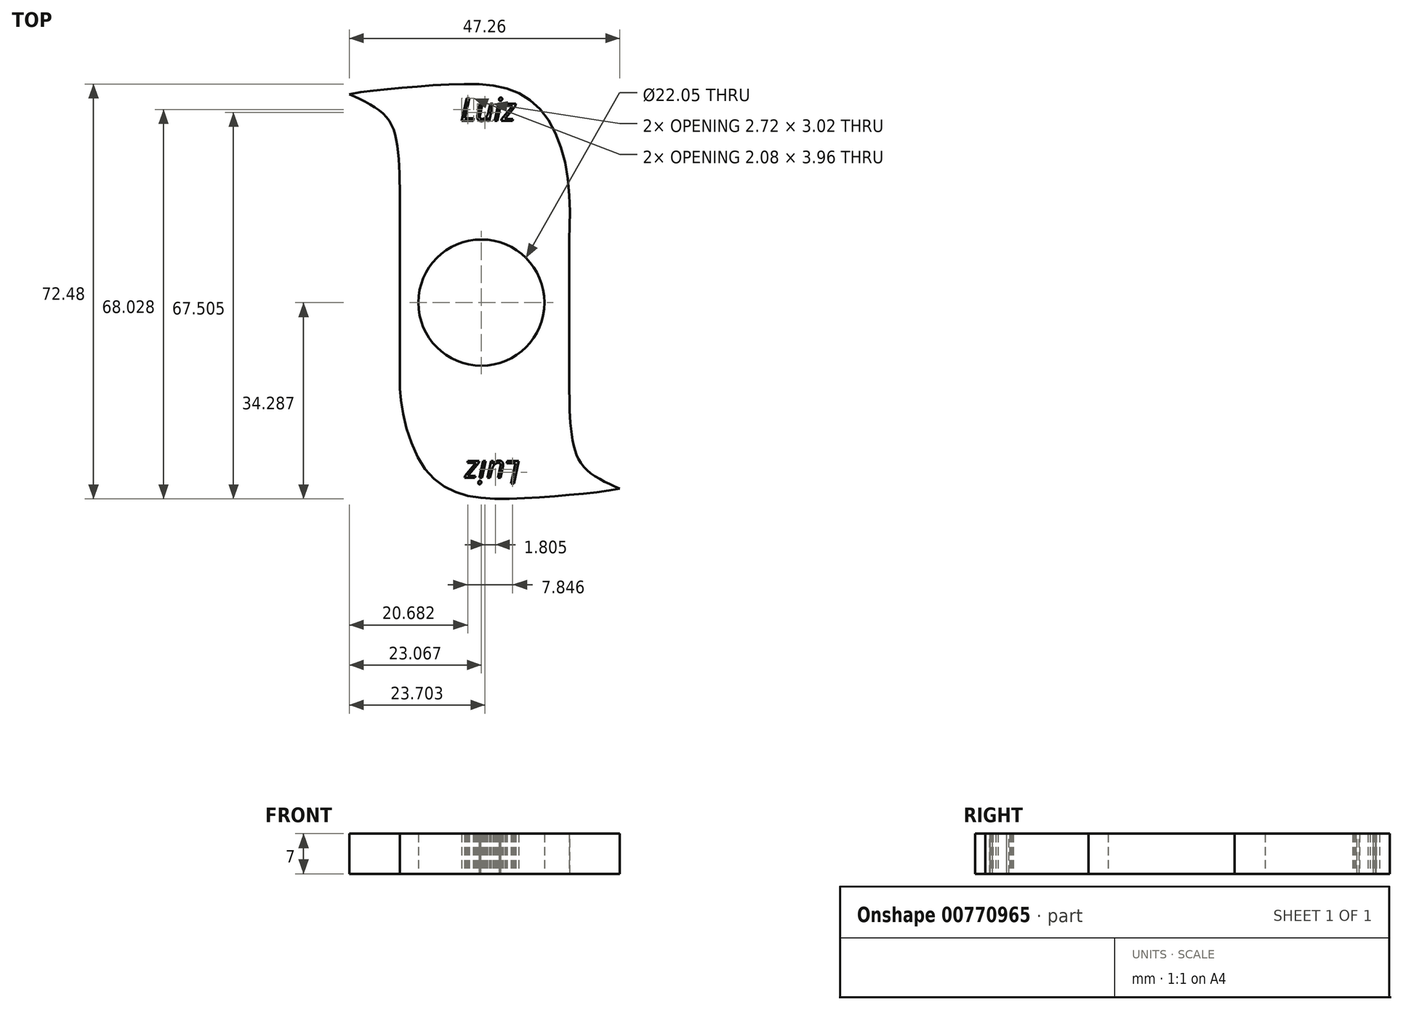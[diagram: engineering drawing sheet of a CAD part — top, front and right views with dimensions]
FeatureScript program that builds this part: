
annotation { "Feature Type Name" : "Feature", "Feature Type Description" : "" }
export const myFeature = defineFeature(function(context is Context, id is Id, definition is map)
    precondition{}
    {
        {
            var Q0;
            Q0=qCreatedBy(makeId("Top.planeOp"),FACE);
            var sketch = newSketch(context, id + "F0", { "sketchPlane" : qUnion([Q0])});
            skFitSpline(sketch, "E0", {"points": [v(-50.4, 39.12) * mm, v(-46.36, 40.38) * mm, v(-38.53, 41.4) * mm, v(-27.4, 42.15) * mm, v(-18.06, 41.14) * mm, v(-11.74, 36.09) * mm, v(-8.2, 25.72) * mm, v(-7.95, 15.04) * mm], "startDerivative": vector(36.6, 13.52) * mm, "endDerivative": vector(-1.7, -53.47) * mm});
            skLineSegment(sketch, "E1", {"start": v(-7.95, 15.04) * mm, "end": v(-7.95, 3.99) * mm});
            skFitSpline(sketch, "E2", {"points": [v(-46.36, 40.38) * mm, v(-40.3, 36.84) * mm, v(-38.02, 31.54) * mm, v(-37.52, 20.42) * mm], "startDerivative": vector(20.87, -9.1) * mm, "endDerivative": vector(0.32, -24.58) * mm});
            skFitSpline(sketch, "E3", {"points": [v(-37.52, 20.42) * mm, v(-37.52, 15.04) * mm], "startDerivative": vector(0, -5.06) * mm, "endDerivative": vector(0, -5.06) * mm});
            skLineSegment(sketch, "E4", {"start": v(-37.52, 15.04) * mm, "end": v(-37.52, 3.99) * mm});
            skFitSpline(sketch, "E5", {"points": [v(4.94, -27.24) * mm, v(0.9, -28.5) * mm, v(-6.94, -29.52) * mm, v(-18.06, -30.28) * mm, v(-27.4, -29.27) * mm, v(-33.73, -24.21) * mm, v(-37.27, -13.85) * mm, v(-37.52, -7.06) * mm], "startDerivative": vector(-36.6, -13.52) * mm, "endDerivative": vector(1.7, 53.47) * mm});
            skLineSegment(sketch, "E6", {"start": v(-37.52, -7.06) * mm, "end": v(-37.52, 3.99) * mm});
            skFitSpline(sketch, "E7", {"points": [v(0.9, -28.5) * mm, v(-5.17, -24.97) * mm, v(-7.44, -19.66) * mm, v(-7.95, -10.5) * mm], "startDerivative": vector(-20.87, 9.1) * mm, "endDerivative": vector(-0.32, 24.58) * mm});
            skFitSpline(sketch, "E8", {"points": [v(-7.95, -10.5) * mm, v(-7.95, -7.06) * mm], "startDerivative": vector(0, 5.06) * mm, "endDerivative": vector(0, 5.06) * mm});
            skLineSegment(sketch, "E9", {"start": v(-7.95, -7.06) * mm, "end": v(-7.95, 3.99) * mm});
            skCircle(sketch, "E10", {"center": v(-23.3, 3.99) * mm, "radius": 11.03 * mm});
            skText(sketch, "E11", { "text": "Luiz", "fontName": "OpenSans-Italic.ttf"});
            skText(sketch, "E12", { "text": "Luiz", "fontName": "OpenSans-Italic.ttf"});
            const initialGuessF0  = {"E11": [-0.02695, 0.03575, 1, 0, 0.00399], "E12": [-0.01656, -0.02367, -1, 0, 0.00399]};
            skSetInitialGuess(sketch, initialGuessF0);
            skSolve(sketch);
        }
        {
            var Q0;
            Q0 = qSketchRegion(id + "F0", true);
            extrude(context, id + "F1", {"entities" : qUnion([Q0]), "depth" : 7 * mm, "offsetDistance" : 25 * mm});
        }
    });
